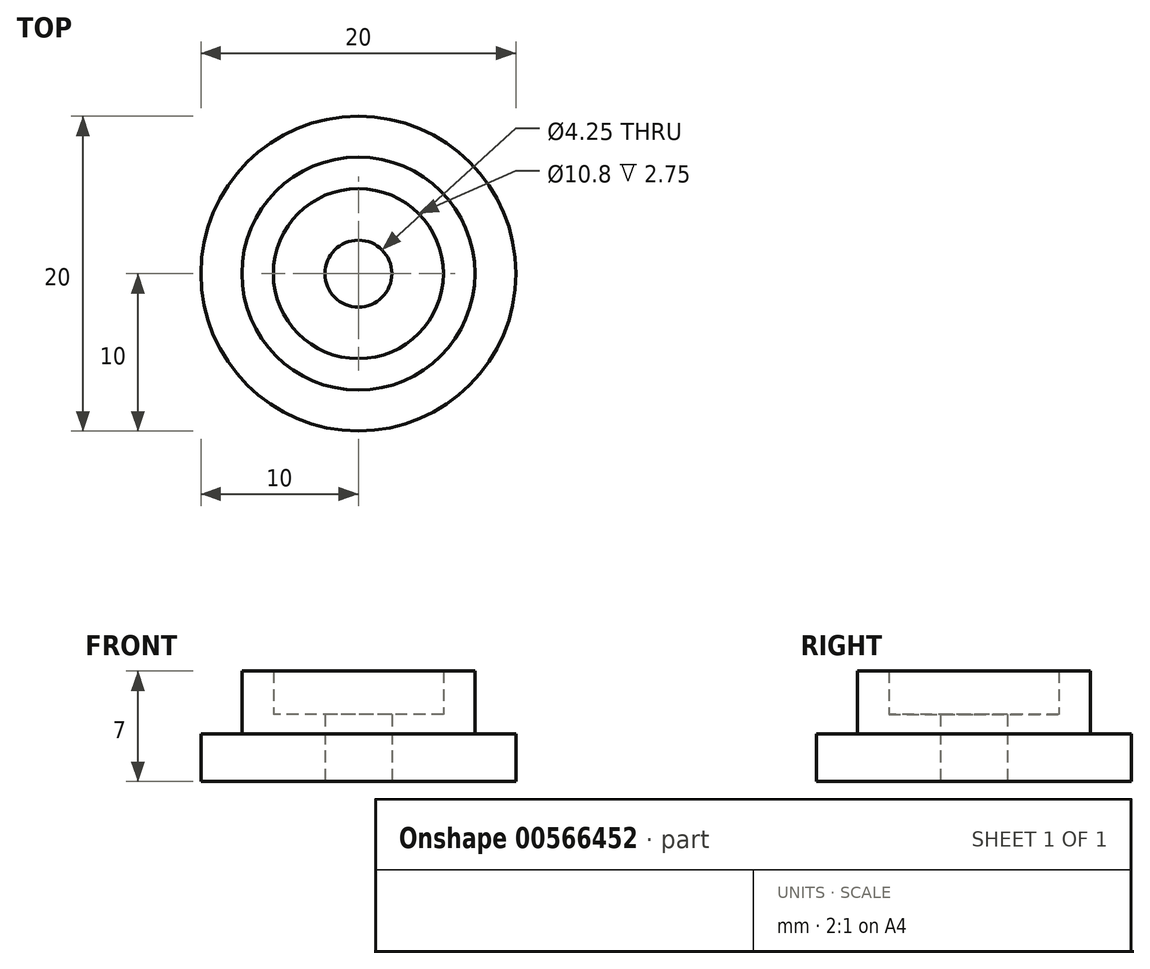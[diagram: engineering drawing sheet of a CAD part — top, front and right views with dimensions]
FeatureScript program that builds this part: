
annotation { "Feature Type Name" : "Feature", "Feature Type Description" : "" }
export const myFeature = defineFeature(function(context is Context, id is Id, definition is map)
    precondition{}
    {
        {
            var Q0;
            Q0=qCreatedBy(makeId("Top.planeOp"),FACE);
            var sketch = newSketch(context, id + "F0", { "sketchPlane" : qUnion([Q0])});
            skCircle(sketch, "E0", {"center": v(0, 0) * mm, "radius": 2.12 * mm});
            skCircle(sketch, "E1", {"center": v(0, 0) * mm, "radius": 5.35 * mm, "construction": true});
            skCircle(sketch, "E2", {"center": v(0, 0) * mm, "radius": 10 * mm});
            skSolve(sketch);
        }
        {
            var Q0;
            Q0=qSketchRegion(id+"F0",true);
            var Q1;
            Q1=sQuery(id+"F0.wireOp",EDGE,"E1");
            extrude(context, id + "F1", {"entities" : qUnion([Q0]), "surfaceEntities" : qUnion([Q1]), "depth" : 3 * mm, "offsetDistance" : 25 * mm});
        }
        {
            var Q0;
            Q0=makeQuery(id+"F1.opExtrude","CAP_FACE",FACE,{"disambiguationData":[OSD([sQuery(id+"F0.wireOp",EDGE,"E0"),sQuery(id+"F0.wireOp",EDGE,"E2")])],"isStart":false});
            var sketch = newSketch(context, id + "F2", { "sketchPlane" : qUnion([Q0])});
            skCircle(sketch, "E3", {"center": v(0, 0) * mm, "radius": 7.4 * mm});
            skCircle(sketch, "E4", {"center": v(0, 0) * mm, "radius": 5.4 * mm});
            skSolve(sketch);
        }
        {
            var Q0;
            Q0=qSketchRegion(id+"F2",true);
            extrude(context, id + "F3", {"entities" : qUnion([Q0]), "operationType" : NewBodyOperationType.ADD, "depth" : 4 * mm, "offsetDistance" : 25 * mm});
        }
        {
            var Q0;
            {var subQ0=sQuery(id+"F0.wireOp",EDGE,"E0");Q0=makeQuery(id+"F3.boolean.opBoolean","SPLIT",FACE,{"disambiguationData":[TD([makeQuery(id+"F1.opExtrude","SWEPT_FACE",FACE,{"disambiguationData":[OSD([subQ0])]})])],"derivedFrom":makeQuery(id+"F1.opExtrude","CAP_FACE",FACE,{"disambiguationData":[OSD([subQ0,sQuery(id+"F0.wireOp",EDGE,"E2")])],"isStart":false})});}
            var sketch = newSketch(context, id + "F4", { "sketchPlane" : qUnion([Q0])});
            skCircle(sketch, "E5", {"center": v(0, 0) * mm, "radius": 2.12 * mm});
            skCircle(sketch, "E6", {"center": v(0, 0) * mm, "radius": 5.4 * mm});
            skSolve(sketch);
        }
        {
            var Q0;
            Q0=qSketchRegion(id+"F4",true);
            extrude(context, id + "F5", {"entities" : qUnion([Q0]), "operationType" : NewBodyOperationType.ADD, "depth" : 1.25 * mm, "offsetDistance" : 25 * mm});
        }
    });
